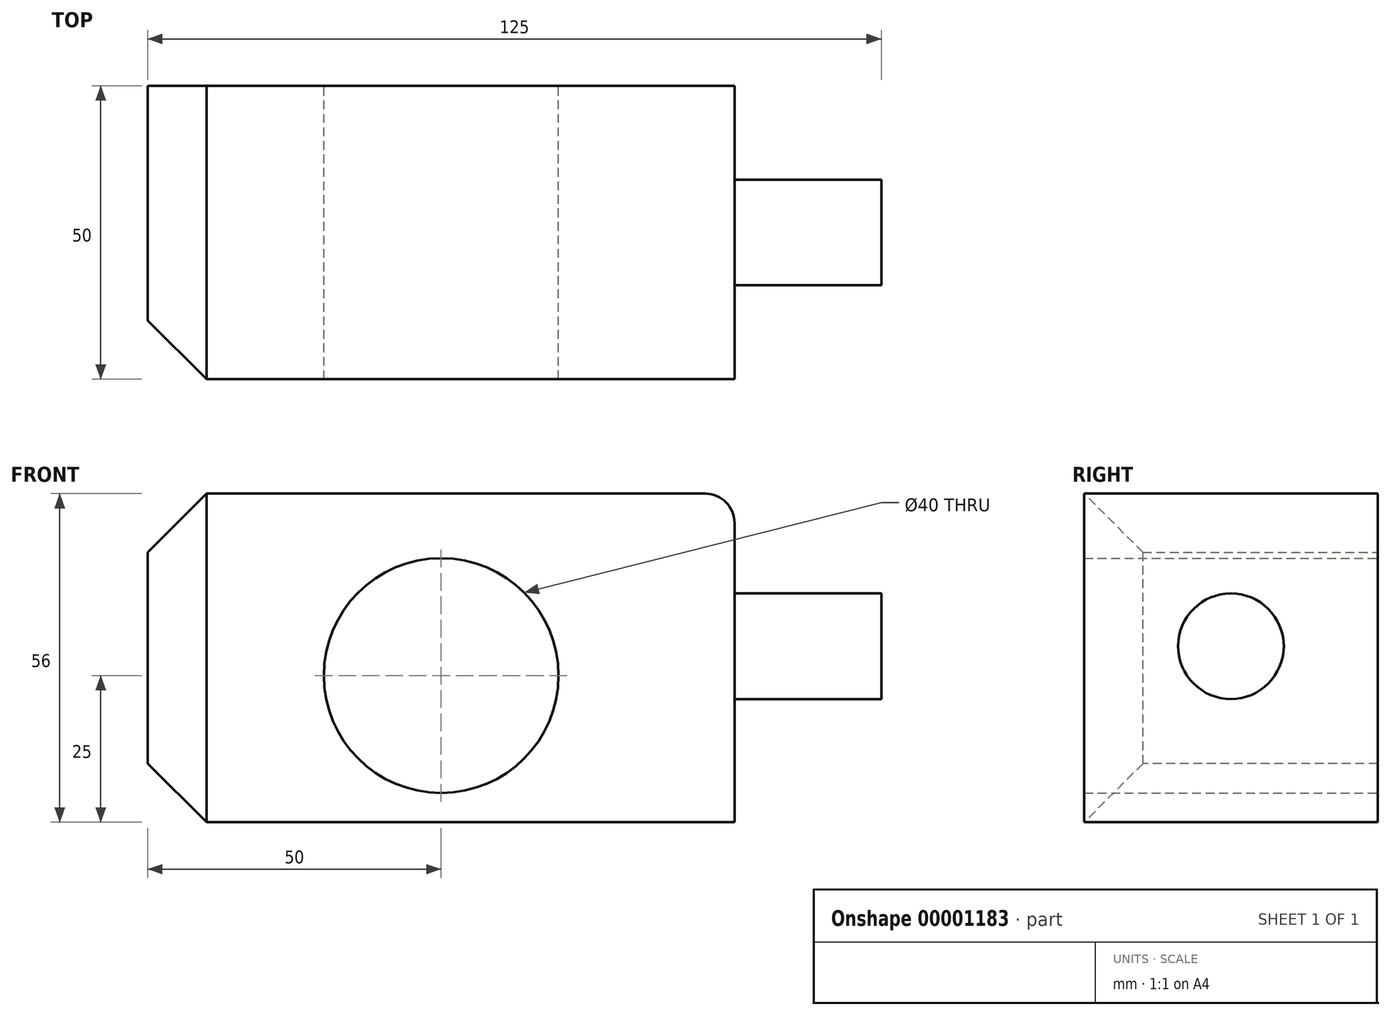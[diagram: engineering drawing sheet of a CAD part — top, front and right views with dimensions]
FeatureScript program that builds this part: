
annotation { "Feature Type Name" : "Feature", "Feature Type Description" : "" }
export const myFeature = defineFeature(function(context is Context, id is Id, definition is map)
    precondition{}
    {
        {
            var Q0;
            Q0=qCreatedBy(makeId("Top.planeOp"),FACE);
            var sketch = newSketch(context, id + "F0", { "sketchPlane" : qUnion([Q0])});
            skLineSegment(sketch, "E0.rect.bottom", {"start": v(50, -25) * mm, "end": v(-50, -25) * mm});
            skLineSegment(sketch, "E0.rect.top", {"start": v(50, 25) * mm, "end": v(-50, 25) * mm});
            skLineSegment(sketch, "E0.rect.left", {"start": v(50, -25) * mm, "end": v(50, 25) * mm});
            skLineSegment(sketch, "E0.rect.right", {"start": v(-50, -25) * mm, "end": v(-50, 25) * mm});
            skPoint(sketch, "E0.rect.middle", {"position": v(0, 0) * mm});
            skSolve(sketch);
        }
        {
            var Q0;
            Q0 = qSketchRegion(id + "F0", true);
            extrude(context, id + "F1", {"entities" : qUnion([Q0]), "depth" : 56 * mm});
        }
        {
            var Q0;
            Q0=makeQuery(id+"F1.opExtrude","CAP_EDGE",EDGE,{"disambiguationData":[OSD([sQuery(id+"F0.wireOp",EDGE,"E0.rect.left")])],"isStart":false});
            fillet(context, id + "F2", {"entities" : qUnion([Q0]), "radius" : 5 * mm, "tangentPropagation" : true, "allowEdgeOverflow" : false});
        }
        {
            var Q0;
            Q0=makeQuery(id+"F1.opExtrude","SWEPT_EDGE",EDGE,{"disambiguationData":[OSD([sQuery(id+"F0.wireOp",EDGE,"E0.rect.bottom"),sQuery(id+"F0.wireOp",EDGE,"E0.rect.right")])]});
            var Q1;
            Q1=makeQuery(id+"F1.opExtrude","CAP_EDGE",EDGE,{"disambiguationData":[OSD([sQuery(id+"F0.wireOp",EDGE,"E0.rect.right")])],"isStart":false});
            var Q2;
            Q2=makeQuery(id+"F1.opExtrude","CAP_EDGE",EDGE,{"disambiguationData":[OSD([sQuery(id+"F0.wireOp",EDGE,"E0.rect.right")])],"isStart":true});
            chamfer(context, id + "F3", {"entities" : qUnion([Q0, Q1, Q2]), "width" : 10 * mm, "tangentPropagation" : true});
        }
        {
            var Q0;
            Q0=qCreatedBy(makeId("Front.planeOp"),FACE);
            var sketch = newSketch(context, id + "F4", { "sketchPlane" : qUnion([Q0])});
            skCircle(sketch, "E1", {"center": v(0, 25) * mm, "radius": 20 * mm});
            skSolve(sketch);
        }
        {
            var Q0;
            Q0 = qSketchRegion(id + "F4", true);
            var Q1;
            Q1=makeQuery(id+"F1.opExtrude","SWEPT_FACE",FACE,{"disambiguationData":[OSD([sQuery(id+"F0.wireOp",EDGE,"E0.rect.top")])]});
            extrude(context, id + "F5", {"entities" : qUnion([Q0]), "operationType" : NewBodyOperationType.REMOVE, "endBound" : BoundingType.SYMMETRIC, "endBoundEntity" : qUnion([Q1]), "depth" : 100 * mm});
        }
        {
            var Q0;
            Q0=makeQuery(id+"F1.opExtrude","SWEPT_FACE",FACE,{"disambiguationData":[OSD([sQuery(id+"F0.wireOp",EDGE,"E0.rect.left")])]});
            var sketch = newSketch(context, id + "F6", { "sketchPlane" : qUnion([Q0])});
            skCircle(sketch, "E2", {"center": v(0, 30) * mm, "radius": 9 * mm});
            skSolve(sketch);
        }
        {
            var Q0;
            Q0 = qSketchRegion(id + "F6", true);
            extrude(context, id + "F7", {"entities" : qUnion([Q0]), "operationType" : NewBodyOperationType.ADD, "depth" : 25 * mm});
        }
    });
